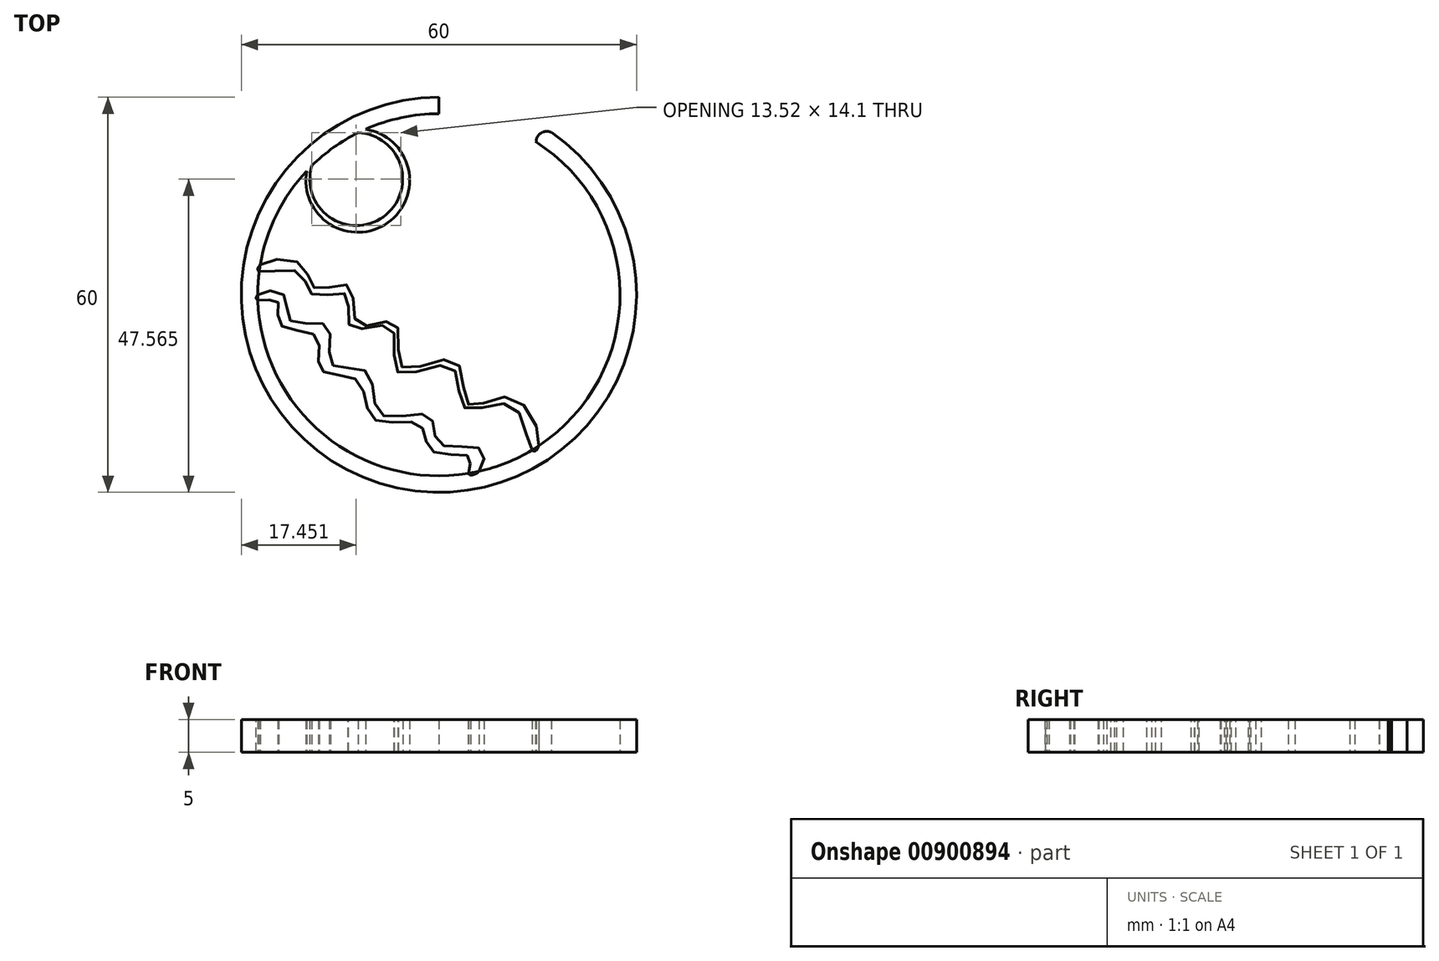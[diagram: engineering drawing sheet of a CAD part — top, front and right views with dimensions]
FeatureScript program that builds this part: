
annotation { "Feature Type Name" : "Feature", "Feature Type Description" : "" }
export const myFeature = defineFeature(function(context is Context, id is Id, definition is map)
    precondition{}
    {
        {
            var Q0;
            Q0=qCreatedBy(makeId("Top.planeOp"),FACE);
            var sketch = newSketch(context, id + "F0", { "sketchPlane" : qUnion([Q0])});
            skCircle(sketch, "E0", {"center": v(0, 0) * mm, "radius": 30 * mm});
            skCircle(sketch, "E1", {"center": v(0, 0) * mm, "radius": 27.5 * mm});
            skFitSpline(sketch, "E2", {"points": [v(14.14, -23.58) * mm, v(11.17, -16.82) * mm, v(3.9, -17.15) * mm, v(1.87, -10.9) * mm, v(-6.24, -11.74) * mm, v(-7.26, -4.98) * mm, v(-13.34, -4.98) * mm, v(-14.02, 0) * mm, v(-19.1, 0) * mm, v(-21.3, 3.47) * mm, v(-27.27, 3.55) * mm, v(-27.12, 4.54) * mm, v(-20.94, 4.65) * mm, v(-18.65, 0.93) * mm, v(-13.61, 1.33) * mm, v(-12.24, -4.5) * mm, v(-6.63, -4.28) * mm, v(-5.6, -10.98) * mm, v(2.42, -10) * mm, v(4.48, -16.64) * mm, v(11.12, -15.61) * mm, v(15.16, -22.94) * mm, v(14.14, -23.58) * mm]});
            skFitSpline(sketch, "E3", {"points": [v(6.06, -26.82) * mm, v(6.3, -23.42) * mm, v(0, -22.57) * mm, v(-1.52, -18.37) * mm, v(-8.84, -18.16) * mm, v(-10.9, -11.76) * mm, v(-16.3, -10.48) * mm, v(-16.87, -4.8) * mm, v(-22.5, -3.94) * mm, v(-23.56, 0) * mm, v(-27.5, 0) * mm, v(-27.49, -0.82) * mm, v(-24.55, -0.95) * mm, v(-24.13, -4.5) * mm, v(-18.58, -6.36) * mm, v(-18.01, -11.33) * mm, v(-12.32, -13.04) * mm, v(-9.9, -18.87) * mm, v(-2.94, -19.72) * mm, v(-1.1, -23.7) * mm, v(4.74, -24.7) * mm, v(4.48, -27.13) * mm, v(6.06, -26.82) * mm]});
            skArc(sketch, "E4", {"start": v(-20.06, 18.8) * mm, "mid": v(-7.76, 10.95) * mm, "end": v(-11.12, 25.15) * mm});
            skArc(sketch, "E5", {"start": v(-19.3, 19.58) * mm, "mid": v(-8.45, 11.83) * mm, "end": v(-12.26, 24.61) * mm});
            skSolve(sketch);
        }
        {
            var Q0;
            Q0=makeQuery(id+"F0.imprint","IMPRINT",FACE,{"disambiguationData":[TD([[makeQuery(id+"F0.imprint","IMPRINT",EDGE,{"derivedFrom":sQuery(id+"F0.wireOp",EDGE,"E0")}),1.0]])]});
            var Q1;
            {var subQ0=sQuery(id+"F0.wireOp",EDGE,"E3");var subQ1=sQuery(id+"F0.wireOp",EDGE,"E1");var subQ2=makeQuery(id+"F0.imprint","INTERSECT",VERTEX,{"disambiguationData":[OD(0.0)],"derivedFrom":[subQ1,subQ0]});Q1=makeQuery(id+"F0.imprint","IMPRINT",FACE,{"disambiguationData":[TD([[makeQuery(id+"F0.imprint","IMPRINT",EDGE,{"disambiguationData":[TD([[subQ2,-1.0]])],"derivedFrom":subQ1}),1.0]])]});}
            var Q2;
            {var subQ0=sQuery(id+"F0.wireOp",EDGE,"E2");var subQ1=sQuery(id+"F0.wireOp",EDGE,"E1");var subQ2=makeQuery(id+"F0.imprint","INTERSECT",VERTEX,{"disambiguationData":[OD(0.0)],"derivedFrom":[subQ1,subQ0]});Q2=makeQuery(id+"F0.imprint","IMPRINT",FACE,{"disambiguationData":[TD([[makeQuery(id+"F0.imprint","IMPRINT",EDGE,{"disambiguationData":[TD([[subQ2,-1.0]])],"derivedFrom":subQ1}),1.0]])]});}
            var Q3;
            {var subQ0=sQuery(id+"F0.wireOp",EDGE,"E4");Q3=makeQuery(id+"F0.imprint","IMPRINT",FACE,{"disambiguationData":[TD([[makeQuery(id+"F0.imprint","IMPRINT",EDGE,{"derivedFrom":subQ0}),1.0]])]});}
            extrude(context, id + "F1", {"entities" : qUnion([Q0, Q1, Q2, Q3]), "endBound" : BoundingType.SYMMETRIC, "depth" : 5 * mm, "offsetDistance" : 25 * mm});
        }
        {
            var Q0;
            Q0=qCreatedBy(makeId("Top.planeOp"),FACE);
            var sketch = newSketch(context, id + "F2", { "sketchPlane" : qUnion([Q0])});
            skLineSegment(sketch, "E6.bottom", {"start": v(0, 32.35) * mm, "end": v(24.66, 32.35) * mm});
            skLineSegment(sketch, "E6.top", {"start": v(0, 25) * mm, "end": v(24.66, 25) * mm});
            skLineSegment(sketch, "E6.left", {"start": v(0, 32.35) * mm, "end": v(0, 25) * mm});
            skLineSegment(sketch, "E6.right", {"start": v(24.66, 32.35) * mm, "end": v(24.66, 25) * mm});
            skSolve(sketch);
        }
        {
            var Q0;
            Q0=makeQuery(id+"F2.imprint","IMPRINT",FACE,{"disambiguationData":[TD([[makeQuery(id+"F2.imprint","IMPRINT",EDGE,{"derivedFrom":sQuery(id+"F2.wireOp",EDGE,"E6.bottom")}),-1.0]])]});
            extrude(context, id + "F3", {"entities" : qUnion([Q0]), "operationType" : NewBodyOperationType.REMOVE, "endBound" : BoundingType.SYMMETRIC, "depth" : 25 * mm, "offsetDistance" : 25 * mm});
        }
        {
            var Q0;
            Q0=qCreatedBy(makeId("Top.planeOp"),FACE);
            var sketch = newSketch(context, id + "F4", { "sketchPlane" : qUnion([Q0])});
            skArc(sketch, "E7", {"start": v(17.24, 24.58) * mm, "mid": v(15.66, 24.65) * mm, "end": v(14.76, 23.35) * mm});
            skLineSegment(sketch, "E8", {"start": v(14.76, 23.35) * mm, "end": v(13.17, 22.47) * mm});
            skLineSegment(sketch, "E9", {"start": v(13.17, 22.47) * mm, "end": v(9.64, 24.94) * mm});
            skLineSegment(sketch, "E10", {"start": v(9.64, 24.94) * mm, "end": v(14.76, 26.7) * mm});
            skLineSegment(sketch, "E11", {"start": v(14.76, 26.7) * mm, "end": v(18.3, 26.7) * mm});
            skLineSegment(sketch, "E12", {"start": v(18.3, 26.7) * mm, "end": v(17.24, 24.58) * mm});
            skSolve(sketch);
        }
        {
            var Q0;
            Q0=makeQuery(id+"F4.imprint","IMPRINT",FACE,{"disambiguationData":[TD([[makeQuery(id+"F4.imprint","IMPRINT",EDGE,{"derivedFrom":sQuery(id+"F4.wireOp",EDGE,"E7")}),-1.0]])]});
            extrude(context, id + "F5", {"entities" : qUnion([Q0]), "operationType" : NewBodyOperationType.REMOVE, "endBound" : BoundingType.SYMMETRIC, "depth" : 25 * mm, "offsetDistance" : 25 * mm});
        }
    });
